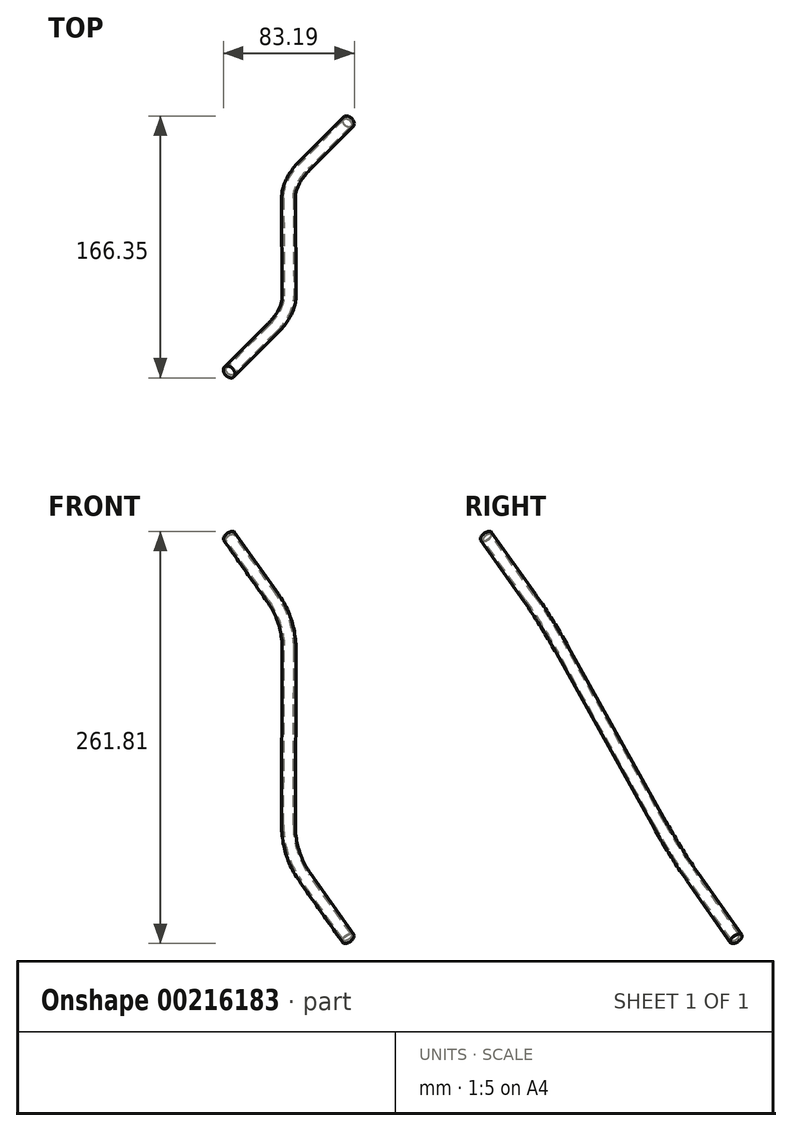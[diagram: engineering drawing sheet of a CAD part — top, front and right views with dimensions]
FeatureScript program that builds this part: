
annotation { "Feature Type Name" : "Feature", "Feature Type Description" : "" }
export const myFeature = defineFeature(function(context is Context, id is Id, definition is map)
    precondition{}
    {
        {
            var Q0;
            Q0=qCreatedBy(makeId("Top.planeOp"),FACE);
            var sketch = newSketch(context, id + "F0", { "sketchPlane" : qUnion([Q0])});
            skLineSegment(sketch, "E0", {"start": v(0, 0) * mm, "end": v(-285.34, 0) * mm});
            skLineSegment(sketch, "E1", {"start": v(-285.34, 0) * mm, "end": v(-285.34, 330.03) * mm});
            skLineSegment(sketch, "E2", {"start": v(0, 0) * mm, "end": v(-361.02, 0) * mm});
            skLineSegment(sketch, "E3", {"start": v(-361.02, 0) * mm, "end": v(-361.02, 171.2) * mm});
            skLineSegment(sketch, "E4", {"start": v(0, 0) * mm, "end": v(-185.8, 0) * mm});
            skLineSegment(sketch, "E5", {"start": v(-185.8, 0) * mm, "end": v(-185.8, 258.16) * mm});
            skSolve(sketch);
        }
        {
            var Q0;
            Q0=sQuery(id+"F0.wireOp",EDGE,"E1");
            cPlane(context, id + "F1", {"entities" : qUnion([Q0]), "cplaneType" : CPlaneType.LINE_ANGLE, "offset" : 25.4 * mm, "angle" : 90 * degree, "width" : 152.4 * mm, "height" : 152.4 * mm});
        }
        {
            var Q0;
            Q0=sQuery(id+"F0.wireOp",EDGE,"E3");
            cPlane(context, id + "F2", {"entities" : qUnion([Q0]), "cplaneType" : CPlaneType.LINE_ANGLE, "offset" : 25.4 * mm, "angle" : 90 * degree, "width" : 152.4 * mm, "height" : 152.4 * mm});
        }
        {
            var Q0;
            Q0=qCreatedBy(id+"F1.planeOp",FACE);
            var sketch = newSketch(context, id + "F3", { "sketchPlane" : qUnion([Q0])});
            skLineSegment(sketch, "E6", {"start": v(330.03, 0) * mm, "end": v(330.03, 731.82) * mm});
            skSolve(sketch);
        }
        {
            var Q0;
            Q0=qCreatedBy(id+"F2.planeOp",FACE);
            var sketch = newSketch(context, id + "F4", { "sketchPlane" : qUnion([Q0])});
            skLineSegment(sketch, "E7", {"start": v(171.2, 0) * mm, "end": v(171.2, 987.49) * mm});
            skSolve(sketch);
        }
        {
            var Q0;
            Q0=sQuery(id+"F0.wireOp",EDGE,"E5");
            cPlane(context, id + "F5", {"entities" : qUnion([Q0]), "cplaneType" : CPlaneType.LINE_ANGLE, "offset" : 25.4 * mm, "angle" : 90 * degree, "width" : 152.4 * mm, "height" : 152.4 * mm});
        }
        {
            var Q0;
            Q0=qCreatedBy(id+"F5.planeOp",FACE);
            var sketch = newSketch(context, id + "F6", { "sketchPlane" : qUnion([Q0])});
            skLineSegment(sketch, "E8", {"start": v(258.16, 0) * mm, "end": v(258.16, 302.16) * mm});
            skSolve(sketch);
        }
        {
            var Q0;
            Q0=sQuery(id+"F6.wireOp",EDGE,"E8");
            var Q1;
            Q1=sQuery(id+"F6.wireOp",VERTEX,"E8.end");
            cPlane(context, id + "F7", {"entities" : qUnion([Q0, Q1]), "cplaneType" : CPlaneType.LINE_POINT, "offset" : 25.4 * mm, "width" : 152.4 * mm, "height" : 152.4 * mm});
        }
        {
            var Q0;
            Q0=qCreatedBy(id+"F7.planeOp",FACE);
            var sketch = newSketch(context, id + "F8", { "sketchPlane" : qUnion([Q0])});
            skArc(sketch, "E9", {"start": v(-507.47, 91.12) * mm, "mid": v(-18.75, -63.51) * mm, "end": v(135.88, 425.2) * mm});
            skLineSegment(sketch, "E10", {"start": v(-507.47, 91.12) * mm, "end": v(-185.8, 258.16) * mm});
            skLineSegment(sketch, "E11", {"start": v(-185.8, 258.16) * mm, "end": v(135.88, 425.2) * mm});
            skSolve(sketch);
        }
        {
            var Q0;
            Q0=sQuery(id+"F3.wireOp",EDGE,"E6");
            cPlane(context, id + "F9", {"entities" : qUnion([Q0]), "cplaneType" : CPlaneType.LINE_ANGLE, "offset" : 25.4 * mm, "angle" : 135 * degree, "width" : 152.4 * mm, "height" : 152.4 * mm});
        }
        {
            var Q0;
            Q0=qCreatedBy(id+"F9.planeOp",FACE);
            var sketch = newSketch(context, id + "F10", { "sketchPlane" : qUnion([Q0])});
            skLineSegment(sketch, "E12", {"start": v(-31.6, 731.82) * mm, "end": v(-133.2, 630.22) * mm});
            skSolve(sketch);
        }
        {
            var Q0;
            Q0=sQuery(id+"F4.wireOp",EDGE,"E7");
            cPlane(context, id + "F11", {"entities" : qUnion([Q0]), "cplaneType" : CPlaneType.LINE_ANGLE, "offset" : 25.4 * mm, "angle" : 135 * degree, "width" : 152.4 * mm, "height" : 152.4 * mm});
        }
        {
            var Q0;
            Q0=qCreatedBy(id+"F11.planeOp",FACE);
            var sketch = newSketch(context, id + "F12", { "sketchPlane" : qUnion([Q0])});
            skLineSegment(sketch, "E13", {"start": v(235.83, 1089.09) * mm, "end": v(134.23, 987.49) * mm});
            skSolve(sketch);
        }
        {
            var Q0;
            Q0=sQuery(id+"F12.wireOp",EDGE,"E13");
            var Q1;
            Q1=sQuery(id+"F12.wireOp",VERTEX,"E13.end");
            cPlane(context, id + "F13", {"entities" : qUnion([Q0, Q1]), "cplaneType" : CPlaneType.LINE_POINT, "offset" : 25.4 * mm, "width" : 152.4 * mm, "height" : 152.4 * mm});
        }
        {
            var Q0;
            Q0=sQuery(id+"F10.wireOp",EDGE,"E12");
            var Q1;
            Q1=sQuery(id+"F10.wireOp",VERTEX,"E12.start");
            cPlane(context, id + "F14", {"entities" : qUnion([Q0, Q1]), "cplaneType" : CPlaneType.LINE_POINT, "offset" : 25.4 * mm, "width" : 152.4 * mm, "height" : 152.4 * mm});
        }
        {
            var Q0;
            Q0=qCreatedBy(id+"F14.planeOp",FACE);
            var sketch = newSketch(context, id + "F15", { "sketchPlane" : qUnion([Q0])});
            skCircle(sketch, "E14", {"center": v(-43.62, -691.98) * mm, "radius": 4.34 * mm});
            skSolve(sketch);
        }
        {
            var Q0;
            Q0=qCreatedBy(id+"F13.planeOp",FACE);
            var sketch = newSketch(context, id + "F16", { "sketchPlane" : qUnion([Q0])});
            skCircle(sketch, "E15", {"center": v(41.07, -709.9) * mm, "radius": 4.34 * mm});
            skSolve(sketch);
        }
        {
            var Q0;
            Q0=qCreatedBy(id+"F9.planeOp",FACE);
            var sketch = newSketch(context, id + "F17", { "sketchPlane" : qUnion([Q0])});
            skLineSegment(sketch, "E16", {"start": v(22.28, 785.7) * mm, "end": v(-31.6, 731.82) * mm});
            skSolve(sketch);
        }
        {
            var Q0;
            Q0=qCreatedBy(id+"F11.planeOp",FACE);
            var sketch = newSketch(context, id + "F18", { "sketchPlane" : qUnion([Q0])});
            skLineSegment(sketch, "E17", {"start": v(134.23, 987.49) * mm, "end": v(80.34, 933.6) * mm});
            skSolve(sketch);
        }
        {
            var Q0;
            Q0=sQuery(id+"F17.wireOp",VERTEX,"E16.start");
            var Q1;
            Q1=sQuery(id+"F18.wireOp",VERTEX,"E17.end");
            var Q2;
            Q2=sQuery(id+"F17.wireOp",VERTEX,"E16.end");
            cPlane(context, id + "F19", {"entities" : qUnion([Q0, Q1, Q2]), "cplaneType" : CPlaneType.THREE_POINT, "offset" : 25.4 * mm, "width" : 152.4 * mm, "height" : 152.4 * mm});
        }
        {
            var Q0;
            Q0=qCreatedBy(id+"F19.planeOp",FACE);
            var sketch = newSketch(context, id + "F20", { "sketchPlane" : qUnion([Q0])});
            skLineSegment(sketch, "E18", {"start": v(-203.68, 564.1) * mm, "end": v(-203.21, 712.59) * mm});
            skLineSegment(sketch, "E19", {"start": v(-193.1, 525.13) * mm, "end": v(-165.01, 477.54) * mm});
            skPoint(sketch, "E20.visualSharp", {"position": v(-203.74, 543.16) * mm});
            skArc(sketch, "E20.filletArc", {"start": v(-203.68, 564.1) * mm, "mid": v(-201.02, 543.9) * mm, "end": v(-193.1, 525.13) * mm});
            skSolve(sketch);
        }
        {
            var Q0;
            Q0=sQuery(id+"F18.wireOp",VERTEX,"E17.start");
            var Q1;
            Q1=sQuery(id+"F18.wireOp",VERTEX,"E17.end");
            var Q2;
            Q2=sQuery(id+"F20.wireOp",VERTEX,"E18.start");
            cPlane(context, id + "F21", {"entities" : qUnion([Q0, Q1, Q2]), "cplaneType" : CPlaneType.THREE_POINT, "offset" : 25.4 * mm, "width" : 152.4 * mm, "height" : 152.4 * mm});
        }
        {
            var Q0;
            Q0=qCreatedBy(id+"F21.planeOp",FACE);
            var sketch = newSketch(context, id + "F22", { "sketchPlane" : qUnion([Q0])});
            skLineSegment(sketch, "E21", {"start": v(-203.68, 564.1) * mm, "end": v(-203.28, 691.65) * mm});
            skLineSegment(sketch, "E22", {"start": v(-213.85, 730.62) * mm, "end": v(-241.94, 778.21) * mm});
            skPoint(sketch, "E23.visualSharp", {"position": v(-203.21, 712.59) * mm});
            skArc(sketch, "E23.filletArc", {"start": v(-203.28, 691.65) * mm, "mid": v(-205.94, 711.85) * mm, "end": v(-213.85, 730.62) * mm});
            skSolve(sketch);
        }
        {
            var Q0;
            Q0=qCreatedBy(id+"F21.planeOp",FACE);
            var sketch = newSketch(context, id + "F23", { "sketchPlane" : qUnion([Q0])});
            skLineSegment(sketch, "E24", {"start": v(-203.68, 564.1) * mm, "end": v(-203.28, 691.65) * mm});
            skSolve(sketch);
        }
        {
            var Q0;
            Q0=makeQuery(id+"F15.imprint","IMPRINT",FACE,{"disambiguationData":[TD([[makeQuery(id+"F15.imprint","IMPRINT",EDGE,{"derivedFrom":sQuery(id+"F15.wireOp",EDGE,"E14")}),1.0]])]});
            var Q1;
            Q1=sQuery(id+"F20.wireOp",EDGE,"E19");
            var Q2;
            Q2=sQuery(id+"F20.wireOp",EDGE,"E20.filletArc");
            var Q3;
            Q3=sQuery(id+"F23.wireOp",EDGE,"E24");
            var Q4;
            Q4=sQuery(id+"F22.wireOp",EDGE,"E23.filletArc");
            var Q5;
            Q5=sQuery(id+"F22.wireOp",EDGE,"E22");
            sweep(context, id + "F24", {"profiles" : qUnion([Q0]), "path" : qUnion([Q1, Q2, Q3, Q4, Q5])});
        }
        {
            var Q0;
            Q0=makeQuery(id+"F24.opSweep","SWEPT_FACE",FACE,{"disambiguationData":[OSD([sQuery(id+"F15.wireOp",EDGE,"E14"),sQuery(id+"F20.wireOp",EDGE,"E19")])]});
            var Q1;
            Q1=makeQuery(id+"F24.opSweep","SWEPT_FACE",FACE,{"disambiguationData":[OSD([sQuery(id+"F15.wireOp",EDGE,"E14"),sQuery(id+"F20.wireOp",EDGE,"E20.filletArc")])]});
            var Q2;
            Q2=makeQuery(id+"F24.opSweep","SWEPT_FACE",FACE,{"disambiguationData":[OSD([sQuery(id+"F15.wireOp",EDGE,"E14"),sQuery(id+"F23.wireOp",EDGE,"E24")])]});
            var Q3;
            Q3=makeQuery(id+"F24.opSweep","SWEPT_FACE",FACE,{"disambiguationData":[OSD([sQuery(id+"F15.wireOp",EDGE,"E14"),sQuery(id+"F22.wireOp",EDGE,"E23.filletArc")])]});
            var Q4;
            Q4=makeQuery(id+"F24.opSweep","SWEPT_FACE",FACE,{"disambiguationData":[OSD([sQuery(id+"F15.wireOp",EDGE,"E14"),sQuery(id+"F22.wireOp",EDGE,"E22")])]});
            var Q5;
            Q5=makeQuery(id+"F24.opSweep","SWEPT_BODY",BODY,{"disambiguationData":[OSD([sQuery(id+"F15.wireOp",EDGE,"E14"),sQuery(id+"F22.wireOp",EDGE,"E22")])]});
            shell(context, id + "F25", {"isHollow" : true, "entities" : qUnion([Q0, Q1, Q2, Q3, Q4]), "parts" : qUnion([Q5]), "thickness" : 1.27 * mm});
        }
    });
